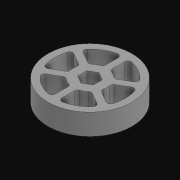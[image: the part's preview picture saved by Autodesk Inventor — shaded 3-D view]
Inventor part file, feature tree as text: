
AUTODESK INVENTOR PART (.ipt)
format: ipt  version: 2021 (Build 250183000, 183)  size: 336,384 bytes
history: native  units: in
note: dims shown in document units (in); Inventor stores cm internally (conversion verified against a paired STEP export)
features: other x9, extrude x2, sketch x2, projected_geometry x2
ambient origin geometry x8: Origin, YZ Plane, XZ Plane, XY Plane, X Axis, Y Axis, Z Axis, Center Point
bodies: Solid1 (feature_tree)
feature tree (15):
  other  "Table"
  other  "Color = 30a Flex Wheel"
  other  "Color = 40a Flex Wheel"
  other  "Thickness = 0.375 in"
  other  "Color = 60a Flex Wheel"
  other  "Thickness = 0.250 in"
  other  "Thickness = 0.125 in"
  other  "Thickness = 0.500 in"
  extrude  "Extrusion1"  Depth=0.5in TaperAngle=0.0deg
  extrude  "Extrusion2"  [1 undecoded]
  sketch  "Sketch1"  dims[d1=0.0in d2=0.5in d3=0.0in]
  projected_geometry  "Projected Loop1"
  sketch  "Sketch2"
  projected_geometry  "Projected Loop2"
  other  "Cut-Extrude2"
note: 1 required parameter value undecoded (feature->parameter linkage not recoverable at this tier; creation-order binding heuristic only, values carry confidence <= 0.55)
